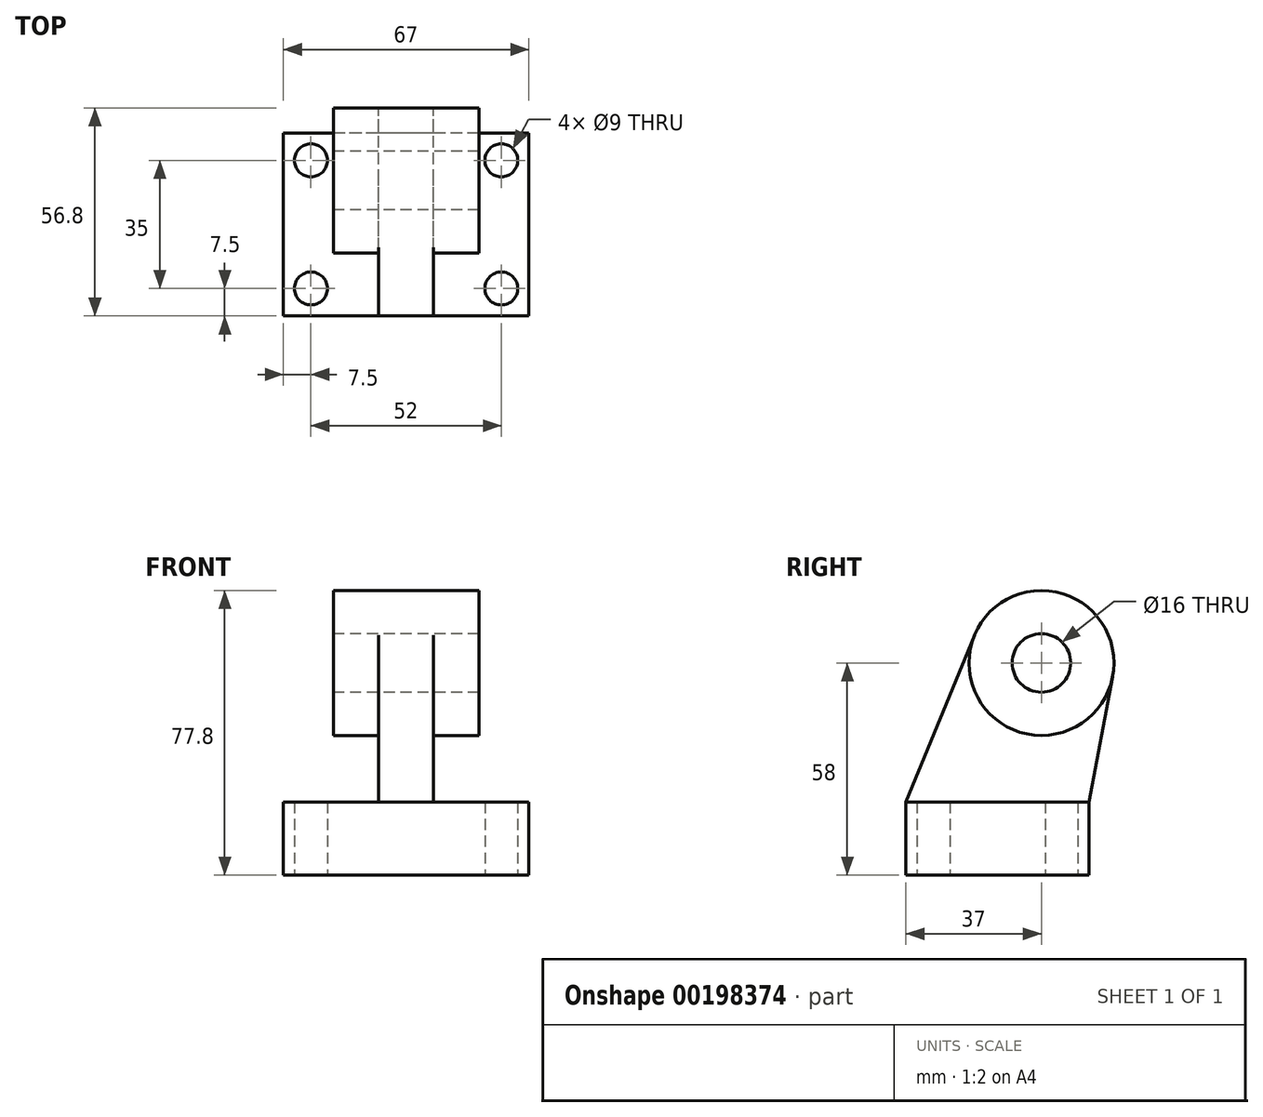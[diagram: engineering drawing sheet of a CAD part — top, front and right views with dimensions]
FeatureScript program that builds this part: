
annotation { "Feature Type Name" : "Feature", "Feature Type Description" : "" }
export const myFeature = defineFeature(function(context is Context, id is Id, definition is map)
    precondition{}
    {
        {
            var Q0;
            Q0=qCreatedBy(makeId("Top.planeOp"),FACE);
            var sketch = newSketch(context, id + "F0", { "sketchPlane" : qUnion([Q0])});
            skLineSegment(sketch, "E0.bottom", {"start": v(33.5, -25) * mm, "end": v(-33.5, -25) * mm});
            skLineSegment(sketch, "E0.top", {"start": v(33.5, 25) * mm, "end": v(-33.5, 25) * mm});
            skLineSegment(sketch, "E0.left", {"start": v(33.5, -25) * mm, "end": v(33.5, 25) * mm});
            skLineSegment(sketch, "E0.right", {"start": v(-33.5, -25) * mm, "end": v(-33.5, 25) * mm});
            skPoint(sketch, "E0.middle", {"position": v(0, 0) * mm});
            skSolve(sketch);
        }
        {
            var Q0;
            Q0 = qSketchRegion(id + "F0", true);
            extrude(context, id + "F1", {"entities" : qUnion([Q0]), "depth" : 20 * mm});
        }
        {
            var Q0;
            Q0=qCreatedBy(makeId("Right.planeOp"),FACE);
            var sketch = newSketch(context, id + "F2", { "sketchPlane" : qUnion([Q0])});
            skCircle(sketch, "E1", {"center": v(12, 58) * mm, "radius": 19.8 * mm});
            skSolve(sketch);
        }
        {
            var Q0;
            Q0 = qSketchRegion(id + "F2", true);
            extrude(context, id + "F3", {"entities" : qUnion([Q0]), "operationType" : NewBodyOperationType.ADD, "endBound" : BoundingType.SYMMETRIC, "depth" : 39.8 * mm});
        }
        {
            var Q0;
            Q0=makeQuery(id+"F3.opExtrude","CAP_FACE",FACE,{"disambiguationData":[OSD([sQuery(id+"F2.wireOp",EDGE,"E1")])],"isStart":true});
            var sketch = newSketch(context, id + "F4", { "sketchPlane" : qUnion([Q0])});
            skCircle(sketch, "E2", {"center": v(-12, 58) * mm, "radius": 8 * mm});
            skSolve(sketch);
        }
        {
            var Q0;
            Q0 = qSketchRegion(id + "F4", true);
            extrude(context, id + "F5", {"entities" : qUnion([Q0]), "operationType" : NewBodyOperationType.REMOVE, "endBound" : BoundingType.THROUGH_ALL, "oppositeDirection" : true, "depth" : 25 * mm});
        }
        {
            var Q0;
            Q0=qCreatedBy(makeId("Right.planeOp"),FACE);
            var sketch = newSketch(context, id + "F6", { "sketchPlane" : qUnion([Q0])});
            skLineSegment(sketch, "E3.0", {"start": v(-25, 20) * mm, "end": v(25, 20) * mm});
            skArc(sketch, "E4.0", {"start": v(-6.32, 65.52) * mm, "mid": v(6.38, 39.01) * mm, "end": v(31.46, 54.34) * mm});
            skLineSegment(sketch, "E5", {"start": v(25, 20) * mm, "end": v(31.46, 54.34) * mm});
            skLineSegment(sketch, "E6", {"start": v(-25, 20) * mm, "end": v(-6.32, 65.52) * mm});
            skSolve(sketch);
        }
        {
            var Q0;
            Q0 = qSketchRegion(id + "F6", true);
            extrude(context, id + "F7", {"entities" : qUnion([Q0]), "operationType" : NewBodyOperationType.ADD, "endBound" : BoundingType.SYMMETRIC, "depth" : 15 * mm});
        }
        {
            var Q0;
            Q0=makeQuery(id+"F1.opExtrude","CAP_FACE",FACE,{"disambiguationData":[OSD([sQuery(id+"F0.wireOp",EDGE,"E0.bottom"),sQuery(id+"F0.wireOp",EDGE,"E0.top"),sQuery(id+"F0.wireOp",EDGE,"E0.left"),sQuery(id+"F0.wireOp",EDGE,"E0.right")])],"isStart":true});
            var sketch = newSketch(context, id + "F8", { "sketchPlane" : qUnion([Q0])});
            skCircle(sketch, "E7", {"center": v(-26, 17.5) * mm, "radius": 4.5 * mm});
            skCircle(sketch, "E8", {"center": v(26, 17.5) * mm, "radius": 4.5 * mm});
            skCircle(sketch, "E9", {"center": v(26, -17.5) * mm, "radius": 4.5 * mm});
            skCircle(sketch, "E10", {"center": v(-26, -17.5) * mm, "radius": 4.5 * mm});
            skSolve(sketch);
        }
        {
            var Q0;
            Q0 = qSketchRegion(id + "F8", true);
            extrude(context, id + "F9", {"entities" : qUnion([Q0]), "operationType" : NewBodyOperationType.REMOVE, "endBound" : BoundingType.UP_TO_NEXT, "oppositeDirection" : true, "depth" : 25 * mm});
        }
    });
